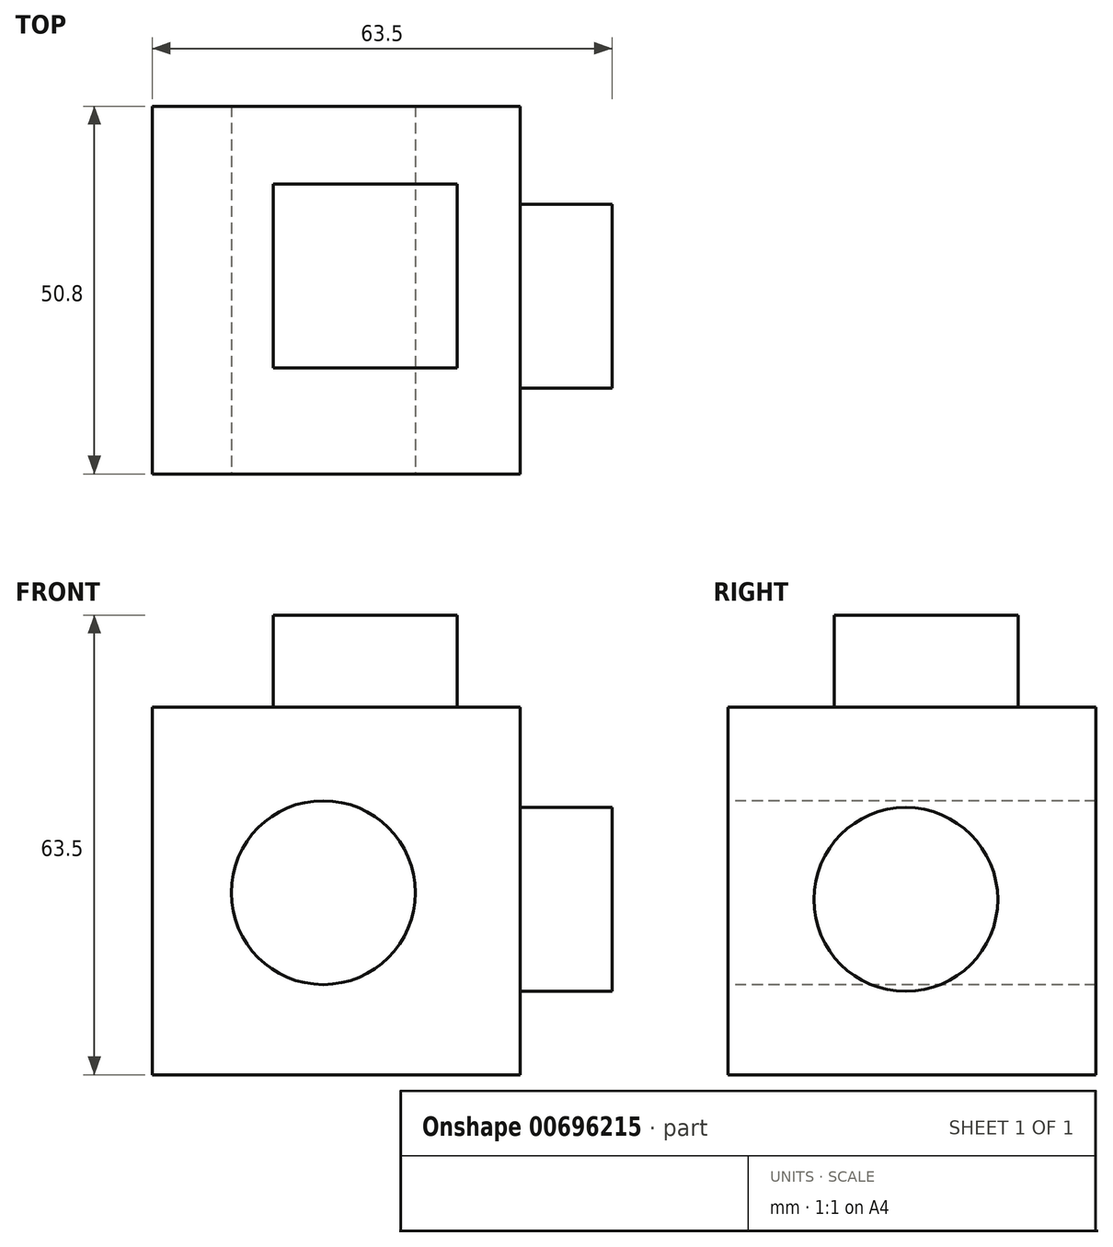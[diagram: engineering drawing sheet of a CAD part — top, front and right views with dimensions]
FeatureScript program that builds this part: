
annotation { "Feature Type Name" : "Feature", "Feature Type Description" : "" }
export const myFeature = defineFeature(function(context is Context, id is Id, definition is map)
    precondition{}
    {
        {
            var Q0;
            Q0=qCreatedBy(makeId("Front.planeOp"),FACE);
            var sketch = newSketch(context, id + "F0", { "sketchPlane" : qUnion([Q0])});
            skLineSegment(sketch, "E0.bottom", {"start": v(0, 0) * mm, "end": v(-50.8, 0) * mm});
            skLineSegment(sketch, "E0.top", {"start": v(0, 50.8) * mm, "end": v(-50.8, 50.8) * mm});
            skLineSegment(sketch, "E0.left", {"start": v(0, 0) * mm, "end": v(0, 50.8) * mm});
            skLineSegment(sketch, "E0.right", {"start": v(-50.8, 0) * mm, "end": v(-50.8, 50.8) * mm});
            skSolve(sketch);
        }
        {
            var Q0;
            Q0=makeQuery(id+"F0.imprint","IMPRINT",FACE,{"disambiguationData":[TD([[makeQuery(id+"F0.imprint","IMPRINT",EDGE,{"derivedFrom":sQuery(id+"F0.wireOp",EDGE,"E0.bottom")}),-1.0]])]});
            extrude(context, id + "F1", {"entities" : qUnion([Q0]), "depth" : 50.8 * mm, "offsetDistance" : 25.4 * mm});
        }
        {
            var Q0;
            Q0=makeQuery(id+"F1.opExtrude","CAP_FACE",FACE,{"disambiguationData":[OSD([sQuery(id+"F0.wireOp",EDGE,"E0.bottom"),sQuery(id+"F0.wireOp",EDGE,"E0.top"),sQuery(id+"F0.wireOp",EDGE,"E0.left"),sQuery(id+"F0.wireOp",EDGE,"E0.right")])],"isStart":false});
            var sketch = newSketch(context, id + "F2", { "sketchPlane" : qUnion([Q0])});
            skCircle(sketch, "E1", {"center": v(-27.2, 25.15) * mm, "radius": 12.7 * mm});
            skSolve(sketch);
        }
        {
            var Q0;
            Q0=makeQuery(id+"F2.imprint","IMPRINT",FACE,{"disambiguationData":[TD([[makeQuery(id+"F2.imprint","IMPRINT",EDGE,{"derivedFrom":sQuery(id+"F2.wireOp",EDGE,"E1")}),1.0]])]});
            var sketch = newSketch(context, id + "F3", { "sketchPlane" : qUnion([Q0])});
            skSolve(sketch);
        }
        {
            var Q0;
            Q0=makeQuery(id+"F3.imprint","IMPRINT",FACE,{"disambiguationData":[TD([[makeQuery(id+"F3.imprint","IMPRINT",EDGE,{"derivedFrom":makeQuery(id+"F2.imprint","IMPRINT",EDGE,{"derivedFrom":sQuery(id+"F2.wireOp",EDGE,"E1")})}),1.0]])]});
            extrude(context, id + "F4", {"entities" : qUnion([Q0]), "operationType" : NewBodyOperationType.REMOVE, "oppositeDirection" : true, "depth" : 50.8 * mm, "offsetDistance" : 25.4 * mm});
        }
        {
            var Q0;
            Q0=makeQuery(id+"F2.imprint","IMPRINT",FACE,{"disambiguationData":[TD([[makeQuery(id+"F2.imprint","IMPRINT",EDGE,{"derivedFrom":sQuery(id+"F2.wireOp",EDGE,"E1")}),1.0]])]});
            extrude(context, id + "F5", {"entities" : qUnion([Q0]), "operationType" : NewBodyOperationType.REMOVE, "oppositeDirection" : true, "depth" : 50.8 * mm, "offsetDistance" : 25.4 * mm});
        }
        {
            var Q0;
            Q0=makeQuery(id+"F1.opExtrude","SWEPT_FACE",FACE,{"disambiguationData":[OSD([sQuery(id+"F0.wireOp",EDGE,"E0.left")])]});
            var sketch = newSketch(context, id + "F6", { "sketchPlane" : qUnion([Q0])});
            skCircle(sketch, "E2", {"center": v(-26.25, 24.2) * mm, "radius": 12.7 * mm});
            skSolve(sketch);
        }
        {
            var Q0;
            Q0=makeQuery(id+"F6.imprint","IMPRINT",FACE,{"disambiguationData":[TD([[makeQuery(id+"F6.imprint","IMPRINT",EDGE,{"derivedFrom":sQuery(id+"F6.wireOp",EDGE,"E2")}),1.0]])]});
            extrude(context, id + "F7", {"entities" : qUnion([Q0]), "operationType" : NewBodyOperationType.ADD, "depth" : 12.7 * mm, "offsetDistance" : 25.4 * mm});
        }
        {
            var Q0;
            Q0=makeQuery(id+"F1.opExtrude","SWEPT_FACE",FACE,{"disambiguationData":[OSD([sQuery(id+"F0.wireOp",EDGE,"E0.top")])]});
            var sketch = newSketch(context, id + "F8", { "sketchPlane" : qUnion([Q0])});
            skLineSegment(sketch, "E3.bottom", {"start": v(-34.11, -36.15) * mm, "end": v(-8.71, -36.15) * mm});
            skLineSegment(sketch, "E3.top", {"start": v(-34.11, -10.75) * mm, "end": v(-8.71, -10.75) * mm});
            skLineSegment(sketch, "E3.left", {"start": v(-34.11, -36.15) * mm, "end": v(-34.11, -10.75) * mm});
            skLineSegment(sketch, "E3.right", {"start": v(-8.71, -36.15) * mm, "end": v(-8.71, -10.75) * mm});
            skSolve(sketch);
        }
        {
            var Q0;
            Q0=makeQuery(id+"F8.imprint","IMPRINT",FACE,{"disambiguationData":[TD([[makeQuery(id+"F8.imprint","IMPRINT",EDGE,{"derivedFrom":sQuery(id+"F8.wireOp",EDGE,"E3.bottom")}),1.0]])]});
            extrude(context, id + "F9", {"entities" : qUnion([Q0]), "operationType" : NewBodyOperationType.ADD, "depth" : 12.7 * mm, "offsetDistance" : 25.4 * mm});
        }
    });
